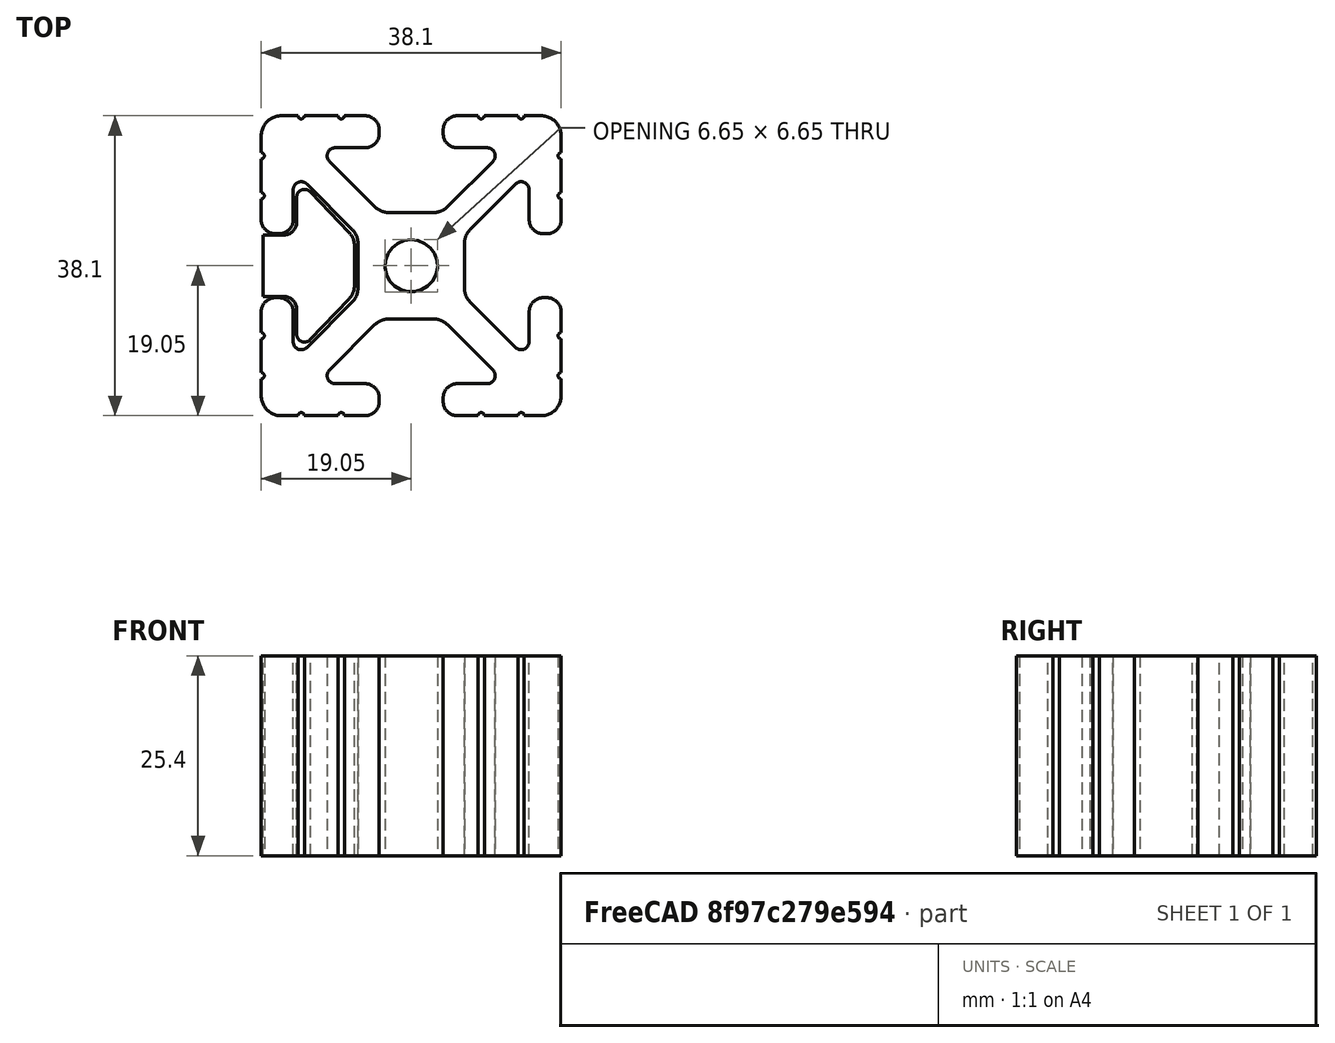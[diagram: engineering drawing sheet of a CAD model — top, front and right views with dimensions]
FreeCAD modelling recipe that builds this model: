
FCSTD DOCUMENT  (FreeCAD 0.18R)
Label: 1515-slot-profile
License: All rights reserved
LicenseURL: http://en.wikipedia.org/wiki/All_rights_reserved
objects: Sketcher::SketchObject×1, PartDesign::Pad×1, PartDesign::Body×1, Part::Feature×1
note: 5 computed .brp shape members not serialized (recipe doc carries the construction recipe); baked Part::Feature solids carry a one-line shape summary decoded from their .brp

FEATURE [Sketcher::SketchObject] Sketch
  sketch-geometry (14):
    g0: LineSegment StartX=-4.25 StartY=3.9 StartZ=0 EndX=-4.25 EndY=-3.9 EndZ=0
    g1: LineSegment StartX=-4.25 StartY=3.9 StartZ=0 EndX=-1.65 EndY=3.9 EndZ=0
    g2: LineSegment StartX=0 StartY=8.7 StartZ=0 EndX=0 EndY=5.55 EndZ=0
    g3: LineSegment StartX=-4.25 StartY=-3.9 StartZ=0 EndX=-1.65 EndY=-3.9 EndZ=0
    g4: ArcOfCircle CenterX=-1.65 CenterY=5.55 CenterZ=0 NormalX=0 NormalY=0 NormalZ=1 AngleXU=0 Radius=1.65 StartAngle=4.71239 EndAngle=6.28319
    g5: ArcOfCircle CenterX=1 CenterY=8.7 CenterZ=0 NormalX=0 NormalY=0 NormalZ=1 AngleXU=0 Radius=1 StartAngle=0.722734 EndAngle=3.14159
    g6: ArcOfCircle CenterX=-1.65 CenterY=-5.55 CenterZ=0 NormalX=0 NormalY=0 NormalZ=1 AngleXU=0 Radius=1.65 StartAngle=0 EndAngle=1.5708
    g7: LineSegment StartX=7.35 StartY=2.5 StartZ=0 EndX=7.35 EndY=-2.5 EndZ=0
    g8: LineSegment StartX=1.75 StartY=9.36144 StartZ=0 EndX=6.66103 EndY=4.219 EndZ=0
    g9: ArcOfCircle CenterX=4.86103 CenterY=2.5 CenterZ=0 NormalX=0 NormalY=0 NormalZ=1 AngleXU=0 Radius=2.48897 StartAngle=0 EndAngle=0.762385
    g10: LineSegment StartX=1.72327 StartY=-9.39057 StartZ=0 EndX=6.66122 EndY=-4.2188 EndZ=0
    g11: ArcOfCircle CenterX=4.86103 CenterY=-2.5 CenterZ=0 NormalX=0 NormalY=0 NormalZ=1 AngleXU=0 Radius=2.48897 StartAngle=5.52091 EndAngle=6.28319
    g12: LineSegment StartX=0 StartY=-5.55 StartZ=0 EndX=0 EndY=-8.7 EndZ=0
    g13: ArcOfCircle CenterX=1 CenterY=-8.7 CenterZ=0 NormalX=0 NormalY=0 NormalZ=1 AngleXU=0 Radius=1 StartAngle=3.14159 EndAngle=5.52091
  constraints (38):
    c: Vertical(g0)
    c: Horizontal(g1)
    c: Vertical(g2)
    c: Horizontal(g3)
    c: Coincident(g1,g0)
    c: Coincident(g3,g0)
    c: Tangent(g1,g4) = -1.5708
    c: Tangent(g2,g4) = 1.5708
    c: Tangent(g2,g5) = -1.5708
    c: Tangent(g3,g6) = 1.5708
    c: DistanceX(g2,g-1) = 0
    c: DistanceY(g-1,g1) = 3.9
    c: DistanceY(g3,g-1) = 3.9
    c: DistanceX(g0,g-1) = 4.25
    c: DistanceX(g6,g-1) = 0
    c: DistanceX(g6,g4) = 0
    c: Vertical(g7)
    c: Tangent(g8,g9) = 1.5708
    c: Tangent(g7,g9) = 1.5708
    c: Coincident(g5,g8)
    c: DistanceX(g4,g-1) = 1.65
    c: DistanceX(g2,g5) = 1
    c: Tangent(g10,g11) = -1.5708
    c: Tangent(g7,g11) = 1.5708
    c: DistanceX(g11,g9) = 0
    c: Vertical(g12)
    c: Tangent(g12,g13) = -1.5708
    c: Tangent(g10,g13) = -1.5708
    c: Coincident(g6,g12)
    c: DistanceX(g5,g13) = 0
    c: DistanceY(g-1,g5) = 8.7
    c: DistanceY(g7,g7) = 5
    c: DistanceX(g9,g8) = 1.8
    c: DistanceY(g-1,g7) = 2.5
    c: DistanceX(g-1,g7) = 7.35
    c: DistanceX(g2,g5) = 1.75
    c: DistanceY(g12,g-1) = 8.7
    c: DistanceY(g6,g-1) = 5.55
FEATURE [PartDesign::Pad] Pad
  Length = 25.4
  Length2 = 100
  Profile = -> Sketch
  Type = 0
FEATURE [PartDesign::Body] Body  label="1515-slot-profile"
  Group = -> [Sketch,Pad]
  Origin = -> Origin
  Tip = -> Pad
FEATURE [Part::Feature] _515_Extrusion
  Placement = pos=(-131.5,-57.15,0) rot=(0,0,1;0rad)
  shape: bbox 38.1 x 38.1 x 25.4 mm, 113 faces (baked)
